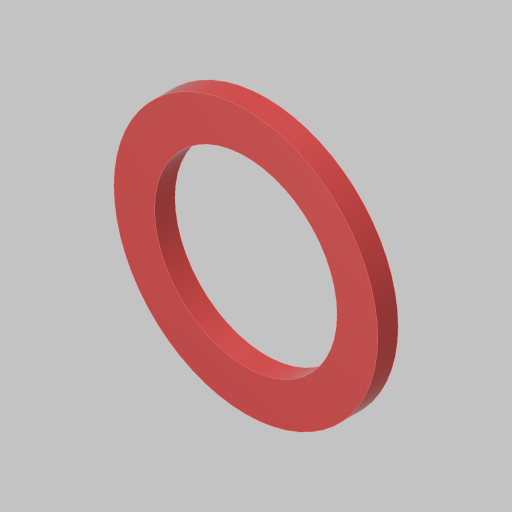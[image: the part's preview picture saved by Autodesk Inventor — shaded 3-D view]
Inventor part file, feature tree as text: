
AUTODESK INVENTOR PART (.ipt)
format: ipt  version: 2023.5 (Build 275446000, 446)  size: 100,864 bytes
history: native  units: in
note: dims shown in document units (in); Inventor stores cm internally (conversion verified against a paired STEP export)
features: extrude x1, sketch x1
ambient origin geometry x8: Origin, YZ Plane, XZ Plane, XY Plane, X Axis, Y Axis, Z Axis, Center Point
bodies: Solid1 (feature_tree)
feature tree (2):
  extrude  "Extrusion1"  Depth=0.0625in
  sketch  "Sketch1"  dims[d0=0.56in d1=0.125in d2=0.0625in d3=0.0in]
